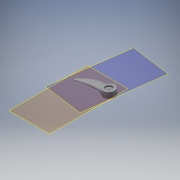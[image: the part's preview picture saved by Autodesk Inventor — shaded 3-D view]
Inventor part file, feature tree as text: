
AUTODESK INVENTOR PART (.ipt)
format: ipt  version: 2019 (Build 230136000, 136)  size: 417,280 bytes
history: native  units: mm
features: other x13, sketch x10, extrude x4, fillet x4, loft x2, revolve x1
ambient origin geometry x8: Origin, YZ Plane, XZ Plane, XY Plane, X Axis, Y Axis, Z Axis, Center Point
bodies: Body1 (feature_tree)
feature tree (34):
  other  "Твердое тело1"
  extrude  "Выдавливание1"  Depth=20.0mm TaperAngle=0.0deg
  other  "РабПлоскость5"
  loft  "Лофт3"
  other  "РабПлоскость6"
  sketch  "Эскиз11"
  revolve  "Вращение2"
  other  "РабПлоскость7"
  sketch  "Эскиз13"
  other  "РабПлоскость8"
  loft  "Лофт4"
  extrude  "Выдавливание5"  TaperAngle=0.0deg  [1 undecoded]
  extrude  "Выдавливание6"  [1 undecoded]
  fillet  "Сопряжение3"  Radius=115.0mm
  fillet  "Сопряжение4"  Radius=3.333333mm
  other  "РабПлоскость9"
  other  "РабПлоскость10"
  sketch  "Эскиз18"
  extrude  "Выдавливание7"  Depth=20.0mm
  fillet  "Сопряжение5"  Radius=40.0mm
  fillet  "Сопряжение6"  Radius=5.0mm
  sketch  "Эскиз1"
  sketch  "Эскиз10"
  other  "Ребра4"
  sketch  "Эскиз12"
  sketch  "Эскиз14"
  other  "Ребра5"
  other  "Ребра6"
  sketch  "Эскиз16"
  sketch  "Эскиз17"
  sketch  "Эскиз19"
  other  "<userpath>\Desktop\RobotFix1\робот\голова - сборка.iam"
  other  "голова - сборка.iam"
  other  "хелицера:2"
note: 2 required parameter values undecoded (feature->parameter linkage not recoverable at this tier; creation-order binding heuristic only, values carry confidence <= 0.55)
